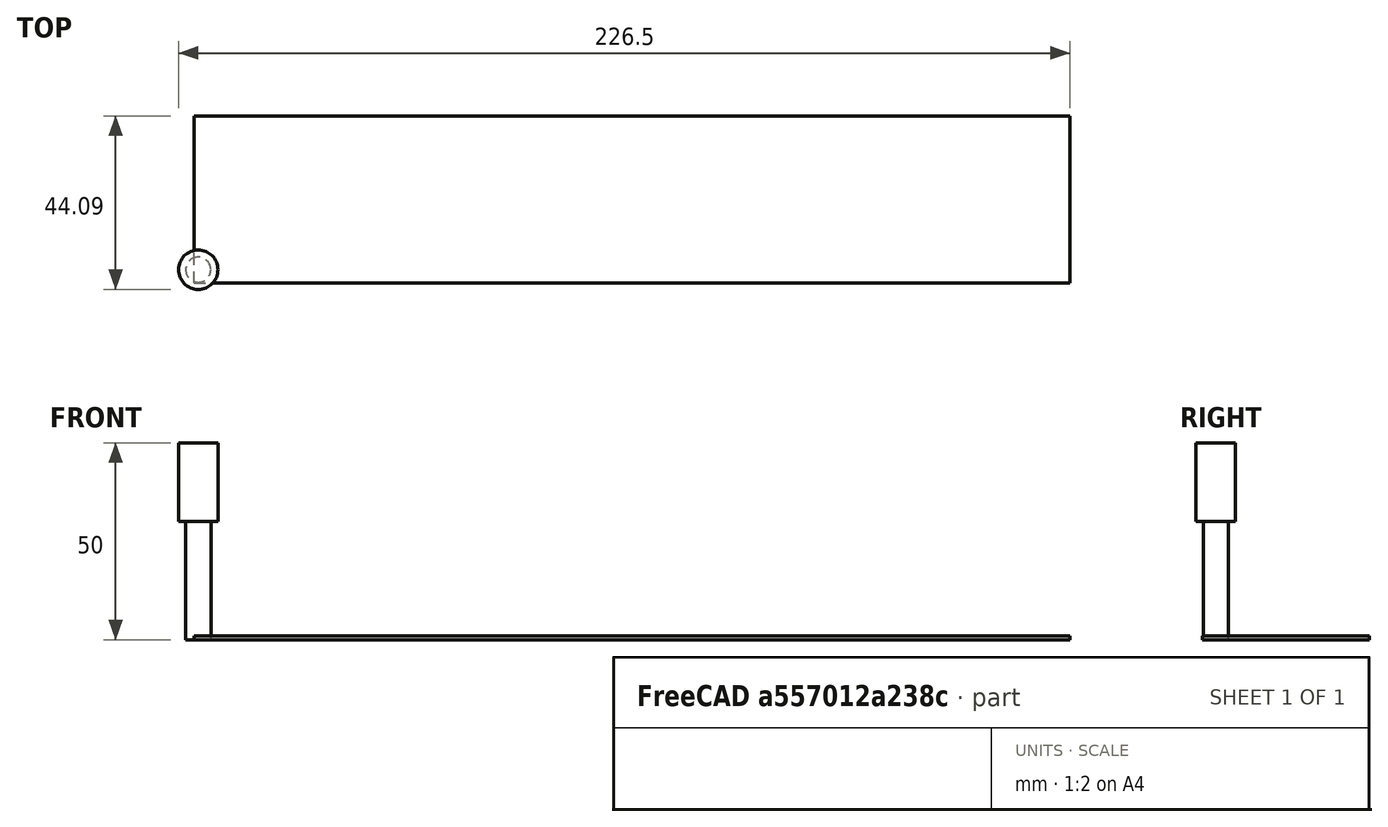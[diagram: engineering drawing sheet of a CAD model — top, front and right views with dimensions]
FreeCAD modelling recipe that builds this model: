
FCSTD DOCUMENT  (FreeCAD 0.20RUnknown)
Label: snake2
License: All rights reserved
LicenseURL: http://en.wikipedia.org/wiki/All_rights_reserved
objects: Part::FeaturePython×3, App::DocumentObjectGroup×3, Path::FeaturePython×3, Part::Part2DObjectPython×1, Part::Offset2D×1, App::FeaturePython×1, Mesh::FeaturePython×1
note: 6 computed .brp shape members not serialized (recipe doc carries the construction recipe); baked Part::Feature solids carry a one-line shape summary decoded from their .brp

FEATURE [Part::Part2DObjectPython] BSpline  # Draft 2D object (typed FeaturePython)
  Area = 0
  Closed = false
  MakeFace = false
  Parameterization = 1
  Points = (34) [(2.2126,11.5408,0),(10.6541,29.5882,0),(18.5135,18.6724,0),(21.861,6.15566,0),(32.4857,9.06654,0),(29.8659,24.4942,0),(34.8144,32.9357,0),+27 more]
FEATURE [Part::Offset2D] Offset2D
  Fill = false
  Intersection = false
  Join = 0
  Mode = 1
  SelfIntersection = false
  Source = -> BSpline
  Value = 3.3
  expr: Value = 3.3mm
FEATURE [App::FeaturePython] SetupSheet  # Path/CAM operation (typed FeaturePython)
  ClearanceHeightExpression = OpStockZMax+SetupSheet.ClearanceHeightOffset
  ClearanceHeightOffset = 5
  CoolantMode = 0
  CoolantModes = None | Flood | Mist
  FinalDepthExpression = OpFinalDepth
  HorizRapid = 0
  SafeHeightExpression = OpStockZMax+SetupSheet.SafeHeightOffset
  SafeHeightOffset = 3
  StartDepthExpression = OpStartDepth
  StepDownExpression = OpToolDiameter
  VertRapid = 0
FEATURE [Part::FeaturePython] Clone  label="Model-Offset2D"  # Draft clone (typed FeaturePython)
  AttacherType = Attacher::AttachEngine3D
  Fuse = false
  Objects = -> [Offset2D]
  PathResource = Model
  Scale = (1,1,1)
FEATURE [App::DocumentObjectGroup] Model
  Group = -> [Clone]
FEATURE [Part::FeaturePython] Stock001  # WARN: FeaturePython — macro-defined, semantics opaque (R4)
  Height = 1
  Length = 222.58
  Placement = pos=(-1.08327,-3.41331,0) rot=(0,0,1;0rad)
  StockType = CreateBox
  Width = 42.5
FEATURE [Part::FeaturePython] ToolBit001  label="6.4mm Endmill"  # Path/CAM toolbit (typed FeaturePython)
  BitPropertyNames = Chipload | CuttingEdgeHeight | Diameter | Flutes | Length | Material | ShankDiameter | SpindleDirection
  BitShape = <path>
  Chipload = 0
  CuttingEdgeHeight = 30
  Diameter = 6.4
  File = <userpath>/Documents/Sherline/FreeCAD/Bit/6.4mm_Endmill.fctb
  Flutes = 0
  Length = 50
  Material = 0
  ShankDiameter = 10
  ShapeName = endmill
  SpindleDirection = 0
FEATURE [Path::FeaturePython] __4mm_Endmill  label="6.4mm Endmill001"  # Path/CAM operation (typed FeaturePython)
  HorizFeed = 15
  HorizRapid = 0
  SpindleDir = 0
  SpindleSpeed = 12000
  Tool = -> ToolBit001
  ToolNumber = 2
  VertFeed = 5
  VertRapid = 0
  expr: HorizRapid = SetupSheet.HorizRapid
  expr: VertRapid = SetupSheet.VertRapid
FEATURE [App::DocumentObjectGroup] Tools
  Group = -> [__4mm_Endmill]
FEATURE [Path::FeaturePython] Profile  # Path/CAM operation (typed FeaturePython)
  Active = true
  AreaParams:
    Tolerance = 1e-07
    FitArcs = True
    Simplify = False
    CleanDistance = 0.0
    Accuracy = 0.01
    Unit = 1.0
    MinArcPoints = 4
    MaxArcPoints = 100
    ClipperScale = 10000000.0
    Fill = 0
    Coplanar = 0
    Reorient = True
    Outline = False
    Explode = False
    OpenMode = 0
    Deflection = 0.01
    SubjectFill = 0
    ClipFill = 0
    Offset = -3.2
    ExtraPass = 0
    Stepover = 0.0
    LastStepover = 0.0
    JoinType = 0
    EndType = 0
    MiterLimit = 2.0
    RoundPrecision = 0.0
    PocketMode = 0
    ToolRadius = 1.0
    PocketExtraOffset = 0.0
    PocketStepover = 0.0
    PocketLastStepover = 0.0
    FromCenter = False
    Angle = 45.0
    AngleShift = 0.0
    Shift = 0.0
    Thicken = False
    SectionCount = -1
    Stepdown = 1.0
    SectionOffset = 0.0
    SectionTolerance = 1e-06
    SectionMode = 2
    Project = False
  Base = -> [Clone]
  ClearanceHeight = 20
  CoolantMode = 0
  CycleTime = 00:02:15
  Direction = 0
  FinalDepth = 0
  HandleMultipleFeatures = 0
  JoinType = 0
  MiterLimit = 0.1
  OffsetExtra = 0
  OpFinalDepth = 0
  OpStartDepth = 1
  OpStockZMax = 1
  OpStockZMin = 0
  OpToolDiameter = 6.4
  PathParams = {'orientation': 1, 'feedrate': 15.0, 'feedrate_v': 5.0, 'verbose': True, 'resume_height': 10.0, 'retraction': 20.0, 'return_end': True, 'preamble': False}
  SafeHeight = 10
  Side = 1
  SplitArcs = false
  StartDepth = 6
  StartPoint = (0,0,0)
  StepDown = 3
  ToolController = -> __4mm_Endmill
  UseComp = true
  UseStartPoint = false
  processCircles = false
  processHoles = false
  processPerimeter = true
  expr: ClearanceHeight = 20
  expr: FinalDepth = OpFinalDepth
  expr: SafeHeight = 10
  expr: StartDepth = 6
  expr: StepDown = 3
FEATURE [App::DocumentObjectGroup] Operations
  Group = -> [Profile]
FEATURE [Path::FeaturePython] Job  # Path/CAM operation (typed FeaturePython)
  CycleTime = 00:02:15
  Fixtures = G54
  GeometryTolerance = 0.01
  JobType = 0
  Model = -> Model
  Operations = -> Operations
  OrderOutputBy = 0
  PostProcessor = 2
  PostProcessorOutputFile = %D/%d.ngc
  SetupSheet = -> SetupSheet
  SplitOutput = false
  Stock = -> Stock001
  Tools = -> Tools
FEATURE [Mesh::FeaturePython] CutMaterial  # WARN: FeaturePython — macro-defined, semantics opaque (R4)
note: 1 file-system path scrubbed to <path> (originals preserved in the JSON sidecar)
